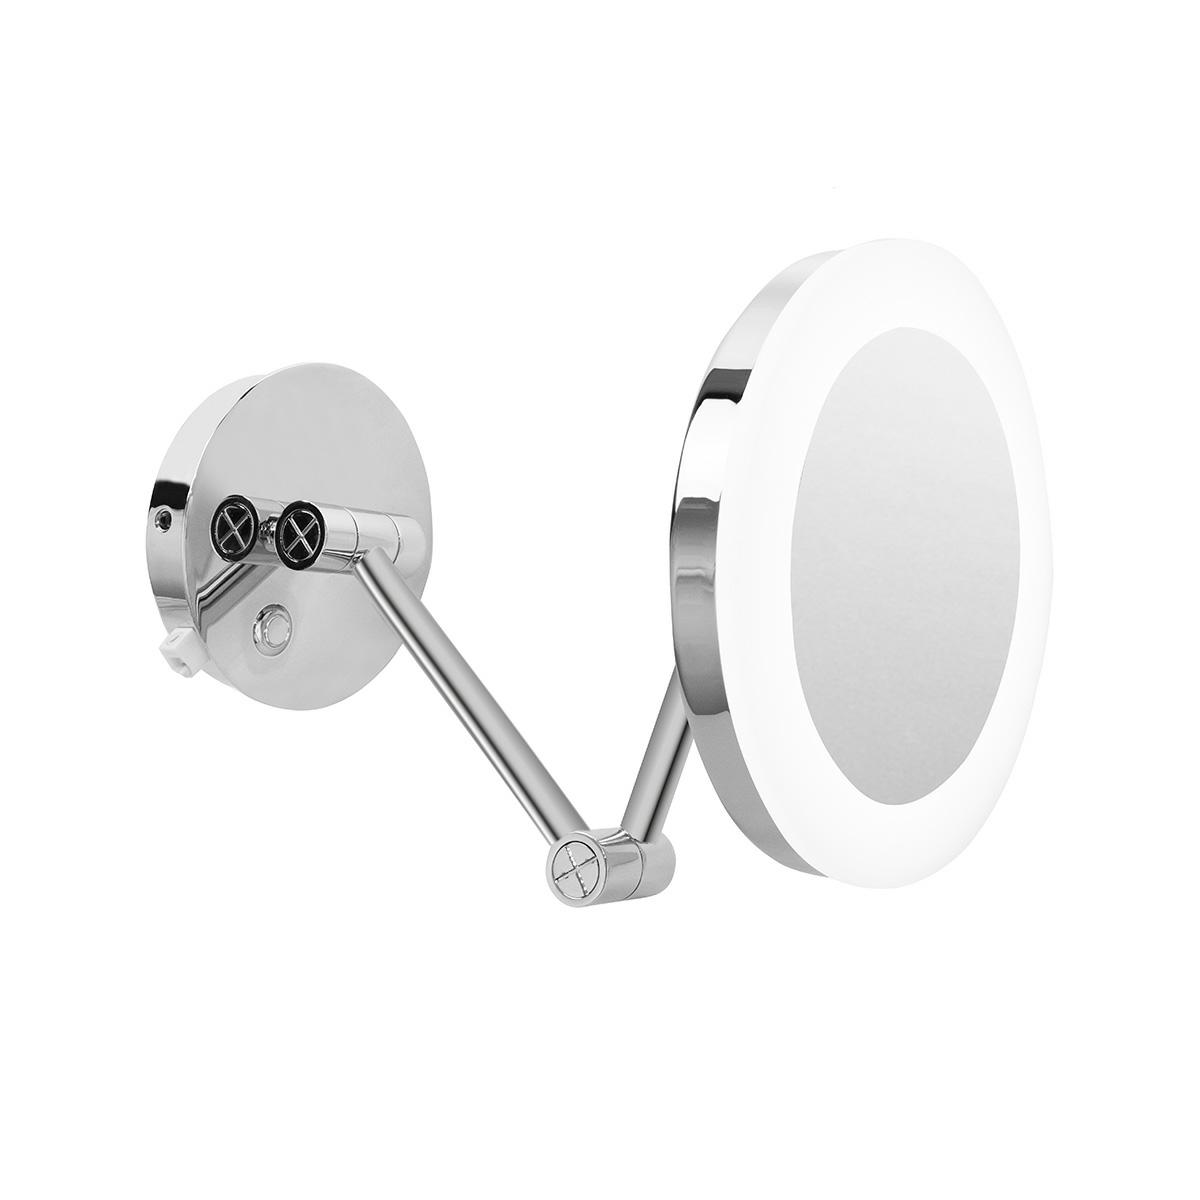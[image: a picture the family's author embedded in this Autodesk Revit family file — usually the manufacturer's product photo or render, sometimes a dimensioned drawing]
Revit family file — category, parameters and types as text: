
# Revit family: ES-003
name_source: partatom
category: Aparatos sanitarios
units: mm (PartAtom-declared; Revit-internal decimal feet)

## family parameters
Compartido = No
Corte con vacíos al cargar = No
Cota de conector redondo = Diámetro de uso
Número OmniClass = 23.45.00.00
Punto de cálculo de habitación = No
Se basa en plano de trabajo = No
Siempre vertical = Sí
Tipo de pieza = Normal
Título OmniClass = Sanitary, Laundry, and Cleaning Equipment

## types (1)
- ES-003
    Comentarios de tipo = Accessories
    Descripción = Espejo retráctil con aumento 3x luz LED
    Elevación por defecto = 0"
    Fabricante = HELVEX
    Features = Espejo retráctil con aumento 3x, luz LED. Acabado cromo
    Feeding Voltage = 100 V
    Imagen de tipo = ES-003.jpg
    Instructive = https://www.helvex.com.mx
    Modelo = ES-003
    Power Consumption = 3 W
    Steel Cap = Steel 1010
    Total Height = 8"
    URL = https://www.helvex.com.mx

## geometry (parser evidence)
native form markers: Sweep x3
no freeform markers — native parametric forms only
